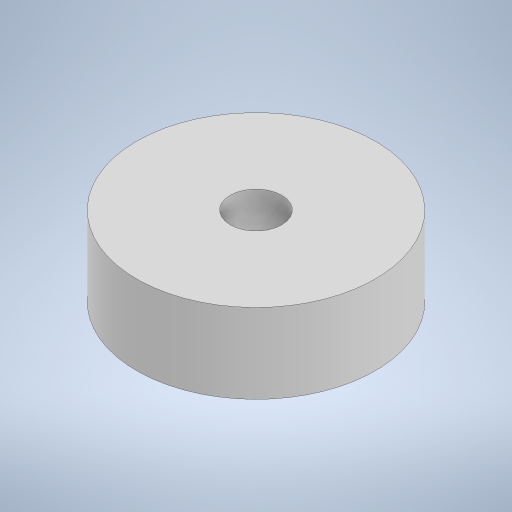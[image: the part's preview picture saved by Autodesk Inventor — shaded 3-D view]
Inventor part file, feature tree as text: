
AUTODESK INVENTOR PART (.ipt)
format: ipt  version: 2023 (Build 270158000, 158)  size: 202,752 bytes
history: native  units: mm
features: extrude x1, sketch x1
ambient origin geometry x8: Origin, YZ Plane, XZ Plane, XY Plane, X Axis, Y Axis, Z Axis, Center Point
bodies: Solid1 (feature_tree)
feature tree (2):
  extrude  "Extrusion1"  Depth=10.0mm
  sketch  "Sketch1"  dims[d0=30.0mm d1=6.469mm d2=10.0mm d3=0.0mm]
